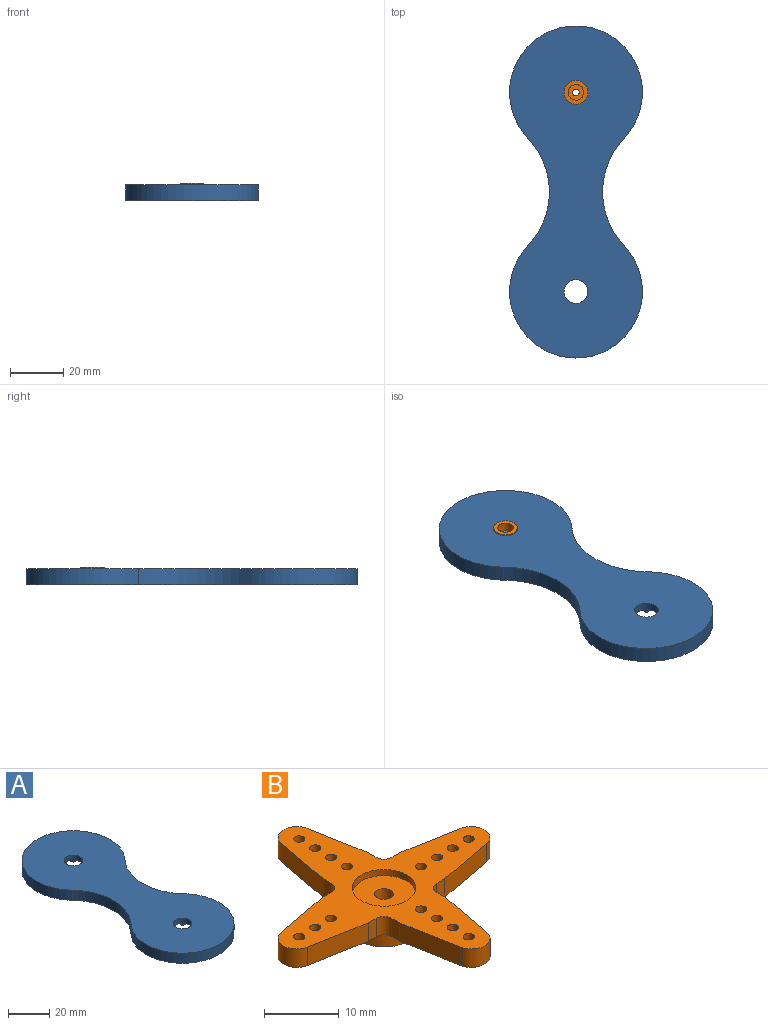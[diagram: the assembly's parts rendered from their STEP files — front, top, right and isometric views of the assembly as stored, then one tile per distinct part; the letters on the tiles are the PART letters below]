
ASSEMBLY  parts=2 mates=1
PART A: 58 faces, bbox 50x125x6 mm
  f0: plane 125x50mm, normal (0,0,1), area 4427.3mm2, adj f3,f4,f6,f7,f56,f57
  f1: plane 39x39mm, normal (0,0,-1), area 468.1mm2, adj f3,f8,f9,f10,f11,f12,f13,f14
  f2: plane 125x50mm, normal (0,0,-1), area 3491.2mm2, adj f4,f7,f8,f9,f10,f11,f12,f13
  f3: cylinder r=4.5mm len=9mm, axis (0,0,-1), area 84.8mm2, adj f0,f1
  f4: cylinder r=25mm len=50mm, axis (0,0,-1), area 699.5mm2, adj f0,f2,f56,f57
  f5: plane 39x39mm, normal (0,0,-1), area 468.1mm2, adj f6,f32,f33,f34,f35,f36,f37,f38
  f6: cylinder r=4.5mm len=9mm, axis (0,0,-1), area 84.8mm2, adj f0,f5
  f7: cylinder r=25mm len=50mm, axis (0,0,-1), area 699.5mm2, adj f0,f2,f56,f57
  f8: cylinder r=1mm len=3mm, axis (0,0,-1), area 4.7mm2, adj f1,f2,f9,f31
  f9: plane 3x1.55mm, normal (-1,0,0), area 4.6mm2, adj f1,f2,f8,f10
  f10: plane 9.75x3mm, normal (-0.98,0.18,0), area 29.7mm2, adj f1,f2,f9,f11
  f11: cylinder r=3mm len=5.9mm, axis (0,0,-1), area 25mm2, adj f1,f2,f10,f12
  f12: plane 9.75x3mm, normal (0.98,0.18,0), area 29.7mm2, adj f1,f2,f11,f13
  f13: plane 3x1.55mm, normal (1,0,0), area 4.6mm2, adj f1,f2,f12,f14
  f14: cylinder r=1mm len=3mm, axis (0,0,-1), area 4.7mm2, adj f1,f2,f13,f15
  f15: plane 3x1.55mm, normal (0,1,0), area 4.6mm2, adj f1,f2,f14,f16
  f16: plane 9.75x3mm, normal (0.18,0.98,0), area 29.7mm2, adj f1,f2,f15,f17
  f17: cylinder r=3mm len=5.9mm, axis (0,0,-1), area 25mm2, adj f1,f2,f16,f18
  f18: plane 9.75x3mm, normal (0.18,-0.98,0), area 29.7mm2, adj f1,f2,f17,f19
  f19: plane 3x1.55mm, normal (0,-1,0), area 4.6mm2, adj f1,f2,f18,f20
  f20: cylinder r=1mm len=3mm, axis (0,0,-1), area 4.7mm2, adj f1,f2,f19,f21
  f21: plane 3x1.55mm, normal (1,0,0), area 4.6mm2, adj f1,f2,f20,f22
  f22: plane 9.75x3mm, normal (0.98,-0.18,0), area 29.7mm2, adj f1,f2,f21,f23
  f23: cylinder r=3mm len=5.9mm, axis (0,0,-1), area 25mm2, adj f1,f2,f22,f24
  f24: plane 9.75x3mm, normal (-0.98,-0.18,0), area 29.7mm2, adj f1,f2,f23,f25
  f25: plane 3x1.55mm, normal (-1,0,0), area 4.6mm2, adj f1,f2,f24,f26
  f26: cylinder r=1mm len=3mm, axis (0,0,-1), area 4.7mm2, adj f1,f2,f25,f27
  f27: plane 3x1.55mm, normal (0,-1,0), area 4.6mm2, adj f1,f2,f26,f28
  f28: plane 9.75x3mm, normal (-0.18,-0.98,0), area 29.7mm2, adj f1,f2,f27,f29
  f29: cylinder r=3mm len=5.9mm, axis (0,0,-1), area 25mm2, adj f1,f2,f28,f30
  f30: plane 9.75x3mm, normal (-0.18,0.98,0), area 29.7mm2, adj f1,f2,f29,f31
  f31: plane 3x1.55mm, normal (0,1,0), area 4.6mm2, adj f1,f2,f8,f30
  f32: cylinder r=1mm len=3mm, axis (0,0,-1), area 4.7mm2, adj f2,f5,f33,f55
  f33: plane 3x1.55mm, normal (0,-1,0), area 4.6mm2, adj f2,f5,f32,f34
  f34: plane 9.75x3mm, normal (-0.18,-0.98,0), area 29.7mm2, adj f2,f5,f33,f35
  f35: cylinder r=3mm len=5.9mm, axis (0,0,-1), area 25mm2, adj f2,f5,f34,f36
  f36: plane 9.75x3mm, normal (-0.18,0.98,0), area 29.7mm2, adj f2,f5,f35,f37
  f37: plane 3x1.55mm, normal (0,1,0), area 4.6mm2, adj f2,f5,f36,f38
  f38: cylinder r=1mm len=3mm, axis (0,0,-1), area 4.7mm2, adj f2,f5,f37,f39
  f39: plane 3x1.55mm, normal (-1,0,0), area 4.6mm2, adj f2,f5,f38,f40
  f40: plane 9.75x3mm, normal (-0.98,0.18,0), area 29.7mm2, adj f2,f5,f39,f41
  f41: cylinder r=3mm len=5.9mm, axis (0,0,-1), area 25mm2, adj f2,f5,f40,f42
  f42: plane 9.75x3mm, normal (0.98,0.18,0), area 29.7mm2, adj f2,f5,f41,f43
  f43: plane 3x1.55mm, normal (1,0,0), area 4.6mm2, adj f2,f5,f42,f44
  f44: cylinder r=1mm len=3mm, axis (0,0,-1), area 4.7mm2, adj f2,f5,f43,f45
  f45: plane 3x1.55mm, normal (0,1,0), area 4.6mm2, adj f2,f5,f44,f46
  f46: plane 9.75x3mm, normal (0.18,0.98,0), area 29.7mm2, adj f2,f5,f45,f47
  f47: cylinder r=3mm len=5.9mm, axis (0,0,-1), area 25mm2, adj f2,f5,f46,f48
  f48: plane 9.75x3mm, normal (0.18,-0.98,0), area 29.7mm2, adj f2,f5,f47,f49
  f49: plane 3x1.55mm, normal (0,-1,0), area 4.6mm2, adj f2,f5,f48,f50
  f50: cylinder r=1mm len=3mm, axis (0,0,-1), area 4.7mm2, adj f2,f5,f49,f51
  f51: plane 3x1.55mm, normal (1,0,0), area 4.6mm2, adj f2,f5,f50,f52
  f52: plane 9.75x3mm, normal (0.98,-0.18,0), area 29.7mm2, adj f2,f5,f51,f53
  f53: cylinder r=3mm len=5.9mm, axis (0,0,-1), area 25mm2, adj f2,f5,f52,f54
  f54: plane 9.75x3mm, normal (-0.98,-0.18,0), area 29.7mm2, adj f2,f5,f53,f55
  f55: plane 3x1.55mm, normal (-1,0,0), area 4.6mm2, adj f2,f5,f32,f54
  f56: cylinder r=29.38mm len=40.52mm, axis (0,0,1), area 268.3mm2, adj f0,f2,f4,f7
  f57: cylinder r=29.38mm len=40.52mm, axis (0,0,1), area 268.3mm2, adj f0,f2,f4,f7
PART B: 48 faces, bbox 38x38x6.5 mm
  f0: cylinder r=1.25mm len=2.5mm, axis (0,0,-1), area 15.7mm2, adj f1,f47
  f1: plane 5.8x5.8mm, normal (0,0,-1), area 21.5mm2, adj f0,f43
  f2: plane 9.7x3mm, normal (0.98,0.18,0), area 29.6mm2, adj f3,f21,f22,f23
  f3: cylinder r=2.5mm len=4.92mm, axis (0,0,-1), area 20.8mm2, adj f2,f4,f22,f23
  f4: plane 9.7x3mm, normal (-0.98,0.18,0), area 29.6mm2, adj f3,f5,f22,f23
  f5: plane 3x1.5mm, normal (-1,0,0), area 4.5mm2, adj f4,f22,f23,f24
  f6: plane 3x1.5mm, normal (0,1,0), area 4.5mm2, adj f7,f22,f23,f24
  f7: plane 9.7x3mm, normal (-0.18,0.98,0), area 29.6mm2, adj f6,f8,f22,f23
  f8: cylinder r=2.5mm len=4.92mm, axis (0,0,-1), area 20.8mm2, adj f7,f9,f22,f23
  f9: plane 9.7x3mm, normal (-0.18,-0.98,0), area 29.6mm2, adj f8,f10,f22,f23
  f10: plane 3x1.5mm, normal (0,-1,0), area 4.5mm2, adj f9,f22,f23,f25
  f11: plane 3x1.5mm, normal (-1,0,0), area 4.5mm2, adj f12,f22,f23,f25
  f12: plane 9.7x3mm, normal (-0.98,-0.18,0), area 29.6mm2, adj f11,f13,f22,f23
  f13: cylinder r=2.5mm len=4.92mm, axis (0,0,-1), area 20.8mm2, adj f12,f14,f22,f23
  f14: plane 9.7x3mm, normal (0.98,-0.18,0), area 29.6mm2, adj f13,f15,f22,f23
  f15: plane 3x1.5mm, normal (1,0,0), area 4.5mm2, adj f14,f22,f23,f26
  f16: plane 3x1.5mm, normal (0,-1,0), area 4.5mm2, adj f17,f22,f23,f26
  f17: plane 9.7x3mm, normal (0.18,-0.98,0), area 29.6mm2, adj f16,f18,f22,f23
  f18: cylinder r=2.5mm len=4.92mm, axis (0,0,-1), area 20.8mm2, adj f17,f19,f22,f23
  f19: plane 9.7x3mm, normal (0.18,0.98,0), area 29.6mm2, adj f18,f20,f22,f23
  f20: plane 3x1.5mm, normal (0,1,0), area 4.5mm2, adj f19,f22,f23,f27
  f21: plane 3x1.5mm, normal (1,0,0), area 4.5mm2, adj f2,f22,f23,f27
  f22: plane 38x38mm, normal (0,0,1), area 383.6mm2, adj f2,f3,f4,f5,f6,f7,f8,f9
  f23: plane 38x38mm, normal (0,0,-1), area 376.7mm2, adj f2,f3,f4,f5,f6,f7,f8,f9
  f24: cylinder r=1.5mm len=3mm, axis (0,0,1), area 7.1mm2, adj f5,f6,f22,f23
  f25: cylinder r=1.5mm len=3mm, axis (0,0,-1), area 7.1mm2, adj f10,f11,f22,f23
  f26: cylinder r=1.5mm len=3mm, axis (0,0,1), area 7.1mm2, adj f15,f16,f22,f23
  f27: cylinder r=1.5mm len=3mm, axis (0,0,-1), area 7.1mm2, adj f20,f21,f22,f23
  f28: cylinder r=0.75mm len=3mm, axis (0,0,1), area 14.1mm2, adj f22,f23
  f29: cylinder r=0.75mm len=3mm, axis (0,0,1), area 14.1mm2, adj f22,f23
  f30: cylinder r=0.75mm len=3mm, axis (0,0,1), area 14.1mm2, adj f22,f23
  f31: cylinder r=0.75mm len=3mm, axis (0,0,1), area 14.1mm2, adj f22,f23
  f32: cylinder r=0.75mm len=3mm, axis (0,0,1), area 14.1mm2, adj f22,f23
  f33: cylinder r=0.75mm len=3mm, axis (0,0,1), area 14.1mm2, adj f22,f23
  f34: cylinder r=0.75mm len=3mm, axis (0,0,1), area 14.1mm2, adj f22,f23
  f35: cylinder r=0.75mm len=3mm, axis (0,0,1), area 14.1mm2, adj f22,f23
  f36: cylinder r=0.75mm len=3mm, axis (0,0,1), area 14.1mm2, adj f22,f23
  f37: cylinder r=0.75mm len=3mm, axis (0,0,1), area 14.1mm2, adj f22,f23
  f38: cylinder r=0.75mm len=3mm, axis (0,0,1), area 14.1mm2, adj f22,f23
  f39: cylinder r=0.75mm len=3mm, axis (0,0,1), area 14.1mm2, adj f22,f23
  f40: cylinder r=0.75mm len=3mm, axis (0,0,1), area 14.1mm2, adj f22,f23
  f41: cylinder r=0.75mm len=3mm, axis (0,0,1), area 14.1mm2, adj f22,f23
  f42: cylinder r=0.75mm len=3mm, axis (0,0,1), area 14.1mm2, adj f22,f23
  f43: cylinder r=2.9mm len=5.8mm, axis (0,0,1), area 63.8mm2, adj f1,f45
  f44: cylinder r=4.5mm len=9mm, axis (0,0,1), area 99mm2, adj f23,f45
  f45: plane 9x9mm, normal (0,0,-1), area 37.2mm2, adj f43,f44
  f46: cylinder r=4.25mm len=8.5mm, axis (0,0,1), area 26.7mm2, adj f22,f47
  f47: plane 8.5x8.5mm, normal (0,0,1), area 51.8mm2, adj f0,f46
PLACE A t=(-59.01,-34.97,-8.6)mm
PLACE B rot(axis=(1,0,0),180deg) t=(-59.01,2.53,-5.6)mm
MATE fastened B.f44 <-> A.f3  axis (0,0,1) through (-59.01,2.53,-5.6)mm
